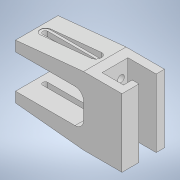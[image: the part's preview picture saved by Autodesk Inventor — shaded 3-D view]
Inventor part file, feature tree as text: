
AUTODESK INVENTOR PART (.ipt)
format: ipt  version: 2022 (Build 260153000, 153)  size: 202,752 bytes
history: native  units: mm
features: extrude x6, sketch x6, projected_geometry x2, hole x1, plane x1, mirror x1, thicken_offset x1
ambient origin geometry x8: Origin, YZ Plane, XZ Plane, XY Plane, X Axis, Y Axis, Z Axis, Center Point
bodies: Solid1 (feature_tree)
feature tree (18):
  extrude  "Extrusion1"  Depth=40.0mm
  sketch  "Sketch2"  dims[d2=20.0mm d3=40.0mm]
  extrude  "Extrusion2"  Depth=40.0mm
  hole  "Hole2"  [1 undecoded]
  extrude  "Extrusion3"  Depth=16.6mm TaperAngle=0.0deg
  extrude  "Extrusion4"  Depth=4.0mm
  extrude  "Extrusion5"  Depth=4.0mm
  plane  "Work Plane1"
  mirror  "Mirror1"
  extrude  "Extrusion6"  Depth=4.0mm
  thicken_offset  "Thicken1"
  sketch  "Sketch1"  dims[d0=6.0mm d1=40.0mm]
  sketch  "Sketch3"  dims[d4=25.0mm d5=0.0mm d6=5.0mm]
  sketch  "Sketch4"  dims[d7=5.0mm d8=16.6mm d9=0.0mm]
  sketch  "Sketch5"  dims[d20=4.0mm d21=6.0mm d22=4.0mm d23=2.0mm d24=90.0deg d25=6.0mm d26=0.0mm d27=5.0mm]
  projected_geometry  "Projected Loop1"
  sketch  "Sketch6"  dims[d28=2.5mm d29=0.0mm d30=4.0mm d31=8.634587mm d32=3.0mm d33=5.0mm d34=5.0mm d35=4.0mm d36=0.0mm d37=1.5mm d38=10.75mm d39=0.0mm d40=4.0mm d41=5.0mm d42=0.0mm d43=0.1mm d44=0.1mm]
  projected_geometry  "Projected Loop2"
note: 1 required parameter value undecoded (feature->parameter linkage not recoverable at this tier; creation-order binding heuristic only, values carry confidence <= 0.55)
